# Revit family: ALDA[1]_вытяжка
name_source: partatom
category: Воздухораспределители
revit_build: Autodesk Revit 2014 (Build: 20130308_1515(x64)
units: mm (PartAtom-declared; Revit-internal decimal feet)

## types (18) — shared parameters
URL = http://inplast.ru
Верх = Нет
Изготовитель = INPLAST-SMAY
Лево = Да
Материал = Алюминий_аннодированный (INPLAST)
Низ = Нет
Описание = Потолочный диффузор односторонний из алюминиевого профиля
Право = Нет
zero-valued in all types: Вес, кг

## per-type parameters (varying)
| type | A | Aef | B | C | C' | D | D' | n | Тип крепежа |
| ALDA 1-150х150-АL | 190 мм | 0.014 м² | 190 мм | 150 мм | 137 мм | 150 мм | 137 мм | 2 | саморезы |
| ALDA 1-205х205-АL | 245 мм | 0.025 м² | 245 мм | 205 мм | 192 мм | 205 мм | 192 мм | 2 | саморезы |
| ALDA 1-261х261-АL | 301 мм | 0.041 м² | 301 мм | 261 мм | 248 мм | 261 мм | 248 мм | 3 | саморезы |
| ALDA 1-317х317-АL | 357 мм | 0.060 м² | 357 мм | 317 мм | 304 мм | 317 мм | 304 мм | 5 | саморезы |
| ALDA 1-372х372-АL | 412 мм | 0.083 м² | 412 мм | 372 мм | 359 мм | 372 мм | 359 мм | 6 | саморезы |
| ALDA 1-429х429-АL | 469 мм | 0.111 м² | 469 мм | 429 мм | 416 мм | 429 мм | 416 мм | 8 | саморезы |
| ALDA 1-458х458-АL | 498 мм | 0.126 м² | 498 мм | 458 мм | 445 мм | 458 мм | 445 мм | 9 | саморезы |
| ALDA 1-558х558-АL | 598 мм | 0.187 м² | 598 мм | 558 мм | 545 мм | 558 мм | 545 мм | 12 | саморезы |
| ALDA 1-583х583-АL | 623 мм | 0.204 м² | 623 мм | 583 мм | 570 мм | 583 мм | 570 мм | 12 | саморезы |
| ALDA 1-150х150-Z-АL | 190 мм | 0.014 м² | 190 мм | 150 мм | 137 мм | 150 мм | 137 мм | 2 | скрытые защелки |
| ALDA 1-205х205-Z-АL | 245 мм | 0.025 м² | 245 мм | 205 мм | 192 мм | 205 мм | 192 мм | 2 | скрытые защелки |
| ALDA 1-261х261-Z-АL | 301 мм | 0.041 м² | 301 мм | 261 мм | 248 мм | 261 мм | 248 мм | 3 | скрытые защелки |
| ALDA 1-317х317-Z-АL | 357 мм | 0.060 м² | 357 мм | 317 мм | 304 мм | 317 мм | 304 мм | 5 | скрытые защелки |
| ALDA 1-372х372-Z-АL | 412 мм | 0.083 м² | 412 мм | 372 мм | 359 мм | 372 мм | 359 мм | 6 | скрытые защелки |
| ALDA 1-429х429-Z-АL | 469 мм | 0.111 м² | 469 мм | 429 мм | 416 мм | 429 мм | 416 мм | 8 | скрытые защелки |
| ALDA 1-458х458-Z-АL | 498 мм | 0.126 м² | 498 мм | 458 мм | 445 мм | 458 мм | 445 мм | 9 | скрытые защелки |
| ALDA 1-558х558-Z-АL | 598 мм | 0.187 м² | 598 мм | 558 мм | 545 мм | 558 мм | 545 мм | 12 | скрытые защелки |
| ALDA 1-583х583-Z-АL | 623 мм | 0.204 м² | 623 мм | 583 мм | 570 мм | 583 мм | 570 мм | 12 | скрытые защелки |

note: column(s) folded — value = type name in every type: Комментарии к типоразмеру
